# Revit family: LAMP_HANCE DOWNLIGHT RECESSED MEDIUM FLOOD 3000_4000
name_source: partatom
category: Modelos genéricos
revit_build: Autodesk Revit 2015 (Build: 20140606_1530(x64)
units: mm (PartAtom-declared; Revit-internal decimal feet)

## types (8) — shared parameters
Altura modulos = 145 mm  [stored 0.475722 ft]
Aro 1000/2000 = No
Aro 3000/4000 = Sí
CRI = 80
Comentarios de tipo = Availability of tilting between 0º and 30º when placed in a project.
Diameter = 188 mm  [stored 0.616798 ft]
Elevación por defecto = 1219 mm
Fabricante = LAMP
Gear = Electronic
IEE = A+
Installation instructions = https://www.lamp.es
Insulation class = II
LED Lifetime = 50.000 L80 B10
Lamp = COB LED
Last update = 21/11/2019
Luminaire type = Indoor - Recessed downlight
MacAdam = 3
Manufacturer URL = http://www.lamp.es
Manufacturer country = Spain
Manufacturer name = LAMP
Material interior aro = LAMP_Aluminio Hance Negro
Model explanation = Availability of tilting between 0º and 30º when placed in a project.
Power Supply = 220-240V 50/60Hz
Product URL = https://www.lamp.es
Product datasheet = http://www.lamp.es
Protection rating = IP20
Radio aro exterior = 49 mm  [stored 0.160761 ft]
Recessed diameter = 175 mm  [stored 0.574147 ft]
Type = COB PHILIPS
Weight = 1.36 kg

## per-type parameters (varying)
| type | Descripción | Efficacy | Finish | Initial color | Initial intensity | Material aro | Modelo | Photometric web file | Plum | Power | Product code |
| 2744LM 4000K 3000 BLACK | HANCE DOWN REC 3000 NW MFL BK. | 99 lm/W | Texturised black RAL 9011 | 4000 K | 2744 lm | LAMP_Aluminio Hance Negro | HD1RE30MF840NBB | Cuerpo Hance BASE (tilting)_MF : 2744LM 4000K 3000 BLACK | 28 W | 25 W | HD1RE30MF840NBB |
| 2744LM 4000K 3000 WHITE | HANCE DOWN REC 3000 NW MFL WH. | 99 lm/W | Texturised white RAL 9010 | 4000 K | 2744 lm | LAMP_Aluminio Hance Blanco | HD1RE30MF840NBW | Cuerpo Hance BASE (tilting)_MF : 2744LM 4000K 3000 WHITE | 28 W | 25 W | HD1RE30MF840NBW |
| 2816LM 3000K 3000 BLACK | HANCE DOWN REC 3000 WW MFL BK. | 100 lm/W | Texturised black RAL 9011 | 3000 K | 2816 lm | LAMP_Aluminio Hance Negro | HD1RE30MF830NBB | Cuerpo Hance BASE (tilting)_MF : 2816LM 3000K 3000 BLACK | 28 W | 25 W | HD1RE30MF830NBB |
| 2816LM 3000K 3000 WHITE | HANCE DOWN REC 3000 WW MFL WH. | 100 lm/W | Texturised white RAL 9010 | 3000 K | 2816 lm | LAMP_Aluminio Hance Blanco | HD1RE30MF830NBW | Cuerpo Hance BASE (tilting)_MF : 2816LM 3000K 3000 WHITE | 28 W | 25 W | HD1RE30MF830NBW |
| 3724LM 3000K 4000 BLACK | HANCE DOWN REC 4000 WW MFL BK. | 99 lm/W | Texturised black RAL 9011 | 3000 K | 3724 lm | LAMP_Aluminio Hance Negro | HD1RE40MF830NBB | Cuerpo Hance BASE (tilting)_MF : 3724LM 3000K 4000 BLACK | 38 W | 34 W | HD1RE40MF830NBB |
| 3724LM 3000K 4000 WHITE | HANCE DOWN REC 4000 WW MFL WH. | 99 lm/W | Texturised white RAL 9010 | 3000 K | 3724 lm | LAMP_Aluminio Hance Blanco | HD1RE40MF830NBW | Cuerpo Hance BASE (tilting)_MF : 3724LM 3000K 4000 WHITE | 38 W | 34 W | HD1RE40MF830NBW |
| 3875LM 4000K 4000 BLACK | HANCE DOWN REC 4000 NW MFL BK. | 103 lm/W | Texturised black RAL 9011 | 4000 K | 3875 lm | LAMP_Aluminio Hance Negro | HD1RE40MF840NBB | Cuerpo Hance BASE (tilting)_MF : 3875LM 4000K 4000 BLACK | 38 W | 34 W | HD1RE40MF840NBB |
| 3875LM 4000K 4000 WHITE | HANCE DOWN REC 4000 NW MFL WH. | 103 lm/W | Texturised white RAL 9010 | 4000 K | 3875 lm | LAMP_Aluminio Hance Blanco | HD1RE40MF840NBW | Cuerpo Hance BASE (tilting)_MF : 3875LM 4000K 4000 WHITE | 38 W | 34 W | HD1RE40MF840NBW |

note: [stored X ft] marks values corroborated as IEEE doubles in the binary element streams (Revit-internal decimal feet)
